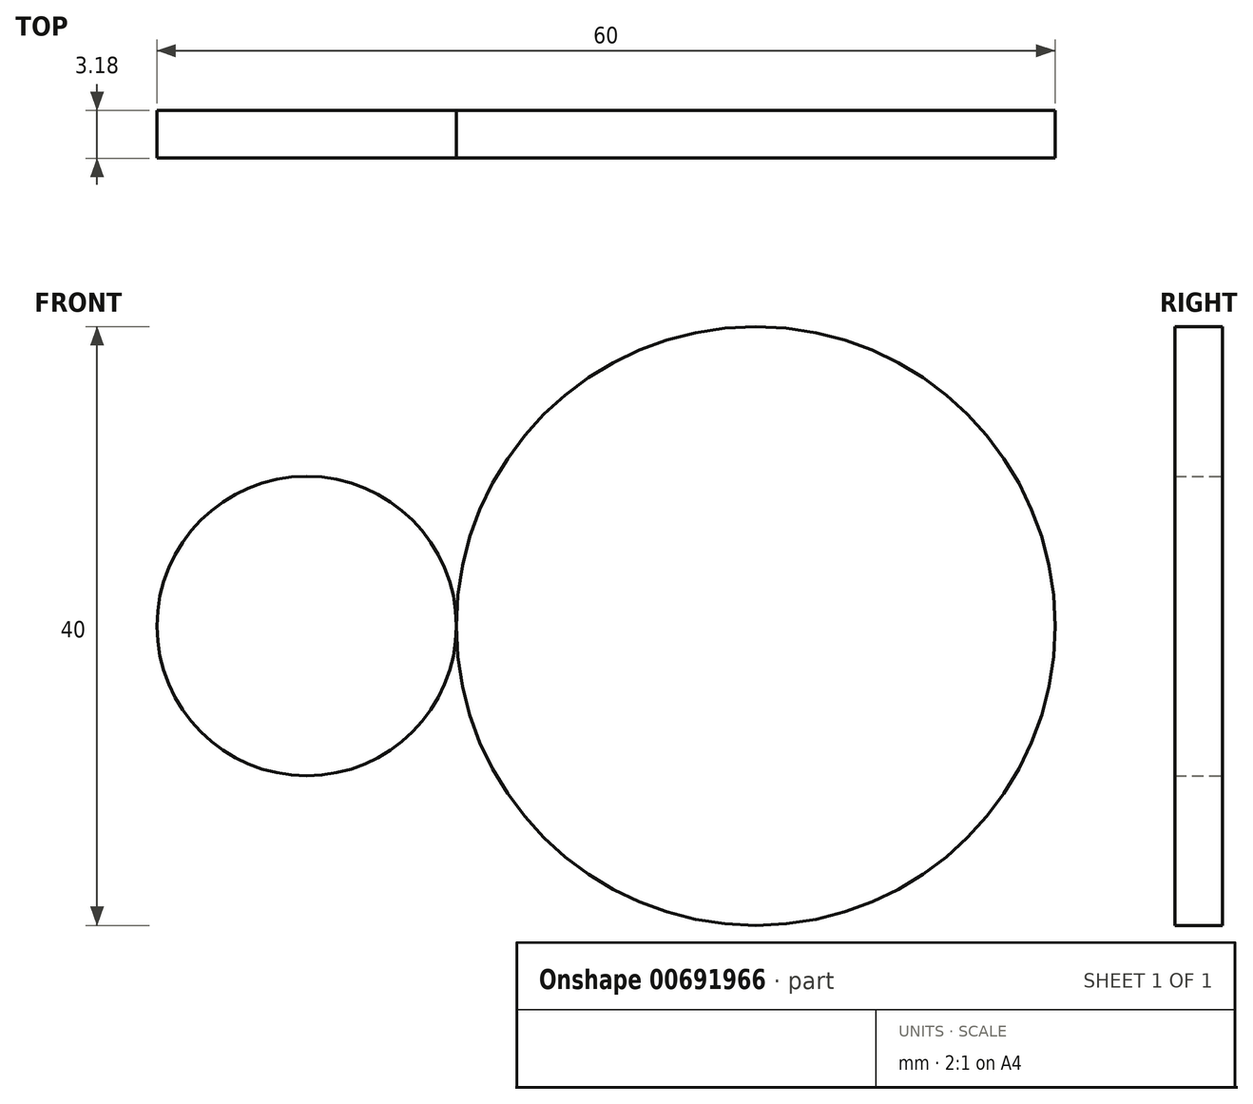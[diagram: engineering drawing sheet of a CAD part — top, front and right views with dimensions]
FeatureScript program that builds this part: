
annotation { "Feature Type Name" : "Feature", "Feature Type Description" : "" }
export const myFeature = defineFeature(function(context is Context, id is Id, definition is map)
    precondition{}
    {
        {
            var Q0;
            Q0=qCreatedBy(makeId("Front.planeOp"),FACE);
            var sketch = newSketch(context, id + "F0", { "sketchPlane" : qUnion([Q0])});
            skCircle(sketch, "E0", {"center": v(0, 0) * mm, "radius": 20 * mm});
            skSolve(sketch);
        }
        {
            var Q0;
            Q0=qCreatedBy(makeId("Front.planeOp"),FACE);
            var sketch = newSketch(context, id + "F1", { "sketchPlane" : qUnion([Q0])});
            skLineSegment(sketch, "E1", {"start": v(0, 0) * mm, "end": v(-30, 0) * mm});
            skCircle(sketch, "E2", {"center": v(-30, 0) * mm, "radius": 10 * mm});
            skSolve(sketch);
        }
        {
            var Q0;
            Q0=makeQuery(id+"F0.imprint","IMPRINT",FACE,{"disambiguationData":[TD([[makeQuery(id+"F0.imprint","IMPRINT",EDGE,{"derivedFrom":sQuery(id+"F0.wireOp",EDGE,"E0")}),1.0]])]});
            var Q1;
            Q1=makeQuery(id+"F1.imprint","IMPRINT",FACE,{"disambiguationData":[TD([[makeQuery(id+"F1.imprint","IMPRINT",EDGE,{"derivedFrom":sQuery(id+"F1.wireOp",EDGE,"E2")}),1.0]])]});
            extrude(context, id + "F2", {"entities" : qUnion([Q0, Q1]), "depth" : 3.17 * mm, "offsetDistance" : 25.4 * mm});
        }
    });
